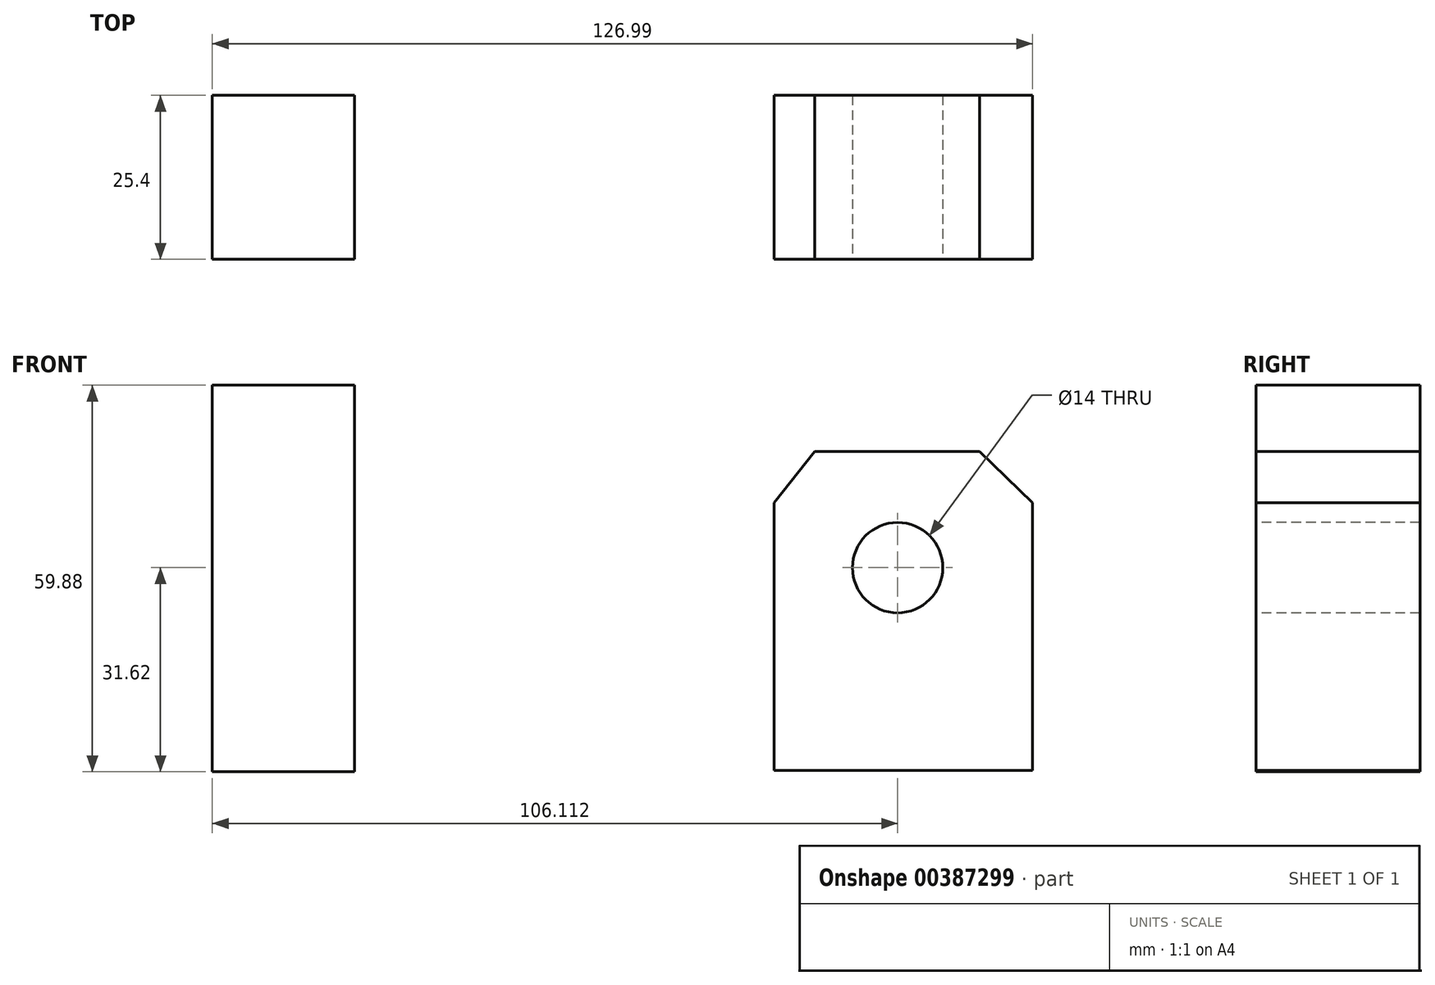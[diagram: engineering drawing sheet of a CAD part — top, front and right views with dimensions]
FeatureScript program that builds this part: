
annotation { "Feature Type Name" : "Feature", "Feature Type Description" : "" }
export const myFeature = defineFeature(function(context is Context, id is Id, definition is map)
    precondition{}
    {
        {
            var Q0;
            Q0=qCreatedBy(makeId("Front.planeOp"),FACE);
            var sketch = newSketch(context, id + "F0", { "sketchPlane" : qUnion([Q0])});
            skLineSegment(sketch, "E0", {"start": v(-63.17, 28.26) * mm, "end": v(-63.17, -31.62) * mm});
            skLineSegment(sketch, "E1", {"start": v(-63.17, -31.62) * mm, "end": v(-41.18, -31.62) * mm});
            skLineSegment(sketch, "E2", {"start": v(-41.18, -31.62) * mm, "end": v(-41.18, 28.26) * mm});
            skLineSegment(sketch, "E3", {"start": v(-41.18, 28.26) * mm, "end": v(-63.17, 28.26) * mm});
            skLineSegment(sketch, "E4", {"start": v(-63.17, 20.98) * mm, "end": v(-41.18, 20.98) * mm});
            skLineSegment(sketch, "E5.bottom", {"start": v(30.07, 18.02) * mm, "end": v(55.65, 18.02) * mm});
            skLineSegment(sketch, "E5.top", {"start": v(23.81, -31.43) * mm, "end": v(63.82, -31.43) * mm});
            skLineSegment(sketch, "E5.left", {"start": v(23.81, 10.07) * mm, "end": v(23.81, -31.43) * mm});
            skLineSegment(sketch, "E5.right", {"start": v(63.82, 10.07) * mm, "end": v(63.82, -31.43) * mm});
            skLineSegment(sketch, "E6", {"start": v(23.81, 10.07) * mm, "end": v(30.07, 18.02) * mm});
            skLineSegment(sketch, "E7", {"start": v(55.65, 18.02) * mm, "end": v(63.82, 10.07) * mm});
            skCircle(sketch, "E8", {"center": v(42.94, 0) * mm, "radius": 7 * mm});
            skSolve(sketch);
        }
        {
            var Q0;
            {var subQ0=sQuery(id+"F0.wireOp",EDGE,"E3");Q0=makeQuery(id+"F0.imprint","IMPRINT",FACE,{"disambiguationData":[TD([[makeQuery(id+"F0.imprint","IMPRINT",EDGE,{"derivedFrom":subQ0}),1.0]])]});}
            var Q1;
            Q1=makeQuery(id+"F0.imprint","IMPRINT",FACE,{"disambiguationData":[TD([[makeQuery(id+"F0.imprint","IMPRINT",EDGE,{"derivedFrom":sQuery(id+"F0.wireOp",EDGE,"E5.top")}),1.0]])]});
            var Q2;
            {var subQ0=sQuery(id+"F0.wireOp",EDGE,"E1");Q2=makeQuery(id+"F0.imprint","IMPRINT",FACE,{"disambiguationData":[TD([[makeQuery(id+"F0.imprint","IMPRINT",EDGE,{"derivedFrom":subQ0}),1.0]])]});}
            extrude(context, id + "F1", {"entities" : qUnion([Q0, Q1, Q2]), "oppositeDirection" : true, "depth" : 25.4 * mm});
        }
    });
